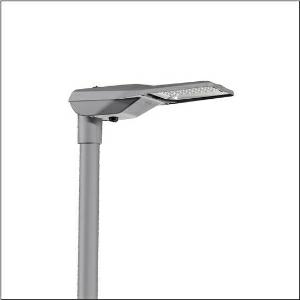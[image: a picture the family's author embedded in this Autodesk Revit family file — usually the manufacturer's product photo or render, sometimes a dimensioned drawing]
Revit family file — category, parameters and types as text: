
# Revit family: streetlight_sl_21_mini___stw1_0a_5xe2e63t08hb_eb5d
name_source: partatom
category: Lighting Fixtures
units: mm (PartAtom-declared; Revit-internal decimal feet)

## family parameters
Cut with Voids When Loaded = No
Host = Face
Light Source = No
Part Type = Normal
Room Calculation Point = No
Round Connector Dimension = Use Diameter
Shared = No

## types (1)
- --- (1 x LED, 8110 lm, 66 W, 2700K)
    Apparent Load = 66 VA
    CIE Flux Codes = 38 75 98 100 100
    Color Rendering = 70
    Color Temperature = 2700K
    Default Elevation = 1800 mm
    Description = Streetlight SL 21 mini, mast luminaire, primary light control with lens, of PMMA, primary optical cover: cover, of toughened safety glass, transparent, light distribution: STW1.0a, light emission: direct distribution, primary light characteristic: asymmetric, installation type: side-entry, post-top, LED, High Power LED, rated luminous flux: 8.110lm, luminous efficacy: 123lm/W, light colour: 727, colour temperature: 2700K, control gear: D4i, control: overheat protection, constant luminous flux control, time-dependent luminous flux control, flexible luminous flux parameterisation, pre-setting: logarithmic dimming characteristic, mains connection: 220..240V, AC, 50/60Hz, start of lifetime: 66W, end of service life: 69W, reduction: 30W, luminaire housing, of diecast aluminium, powder-coated, SITECO metallic grey (DB 702S), corrosivity category C5 high according to DIN EN ISO 12944, please order mast flange separately, inclination adjustable: 0°, 5°, 10°, 15°, sealing non-destructively replaceable, multi-level sealing system, length: 628mm, width: 235mm, height: 110mm, mast flange for spigot size: 42mm (side-entry): 5XC10008XM4, 60/48mm (side-entry/post-top): 5XC10108XM2, 76/60mm (side-entry/post-top): 5XC10108XM1, mounting height: 4..8m, Smart Interface below and above, protection rating (complete): IP66, insulation class (complete): insulation class II (safety insulation), certification: CE, ENEC, ENEC+, VDE, impact resistance: IK10, permissible operating ambient temperature for outdoor applications: -40..+50°C, standard-compliant lighting for roads and squares, packaging unit: 1 piece

Light Distribution: STW1.0a
    Height = 110 mm
    Lamp = 1 x LED
    Lamp Light Flux = 8110 lm
    Lamp Power = 66 W
    Lamp count = 1
    Length = 625 mm
    Luminous efficacy = 123 lm/W
    Manufacturer = Siteco
    ModVariant = No
    Model = 5XE2E63T08HB
    Number of Poles = 1
    OnlyDefault = Yes
    Power Factor = 1
    Product Name = Streetlight SL 21 mini | STW1.0a
    Product group = mast luminaire | pylon top
    ProductGroupID = 6100
    Protection Class = Protection class II
    Protection Degree = IP 66
    RLX_Detail_Level = 1
    RLX_Emergency_Light_Flux = 0 lm
    RLX_Emergency_Type = 0
    RLX_Emergency_Type_DB = No
    RlxData = <blob elided: 26285 chars, md5=70c79df2>
    Socket = socket
    Standby Power = 0 W
    System Light Flux = 8110 lm
    System Power = 66 W
    Type Comments = factory setting: luminous flux: 100 % | dim-lin: 254 | 670 mA
    Type Image = l_1003514.jpg
    URL = http://relux.com
    VarID = @adj_184579
    Voltage = 0 V
    Weight = 0.00 kg
    Width = 234 mm

## geometry (parser evidence)
native form markers: Blend x4, Sweep x11
no freeform markers — native parametric forms only
